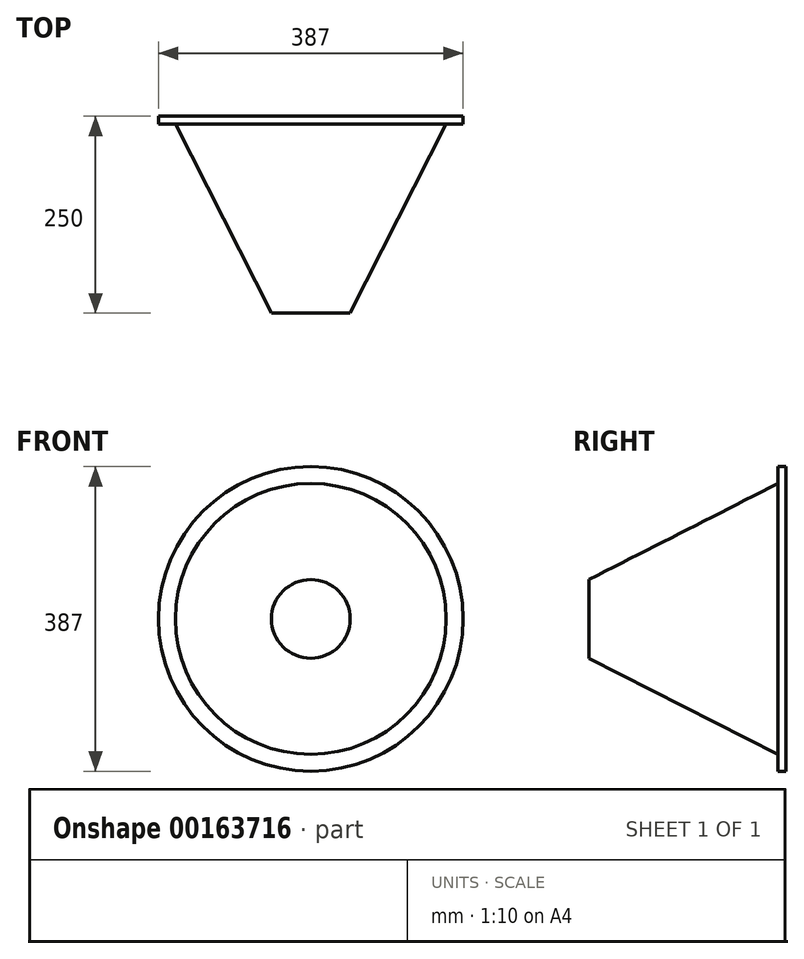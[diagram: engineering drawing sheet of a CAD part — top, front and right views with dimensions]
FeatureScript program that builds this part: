
annotation { "Feature Type Name" : "Feature", "Feature Type Description" : "" }
export const myFeature = defineFeature(function(context is Context, id is Id, definition is map)
    precondition{}
    {
        {
            var Q0;
            Q0=qCreatedBy(makeId("Front.planeOp"),FACE);
            var sketch = newSketch(context, id + "F0", { "sketchPlane" : qUnion([Q0])});
            skCircle(sketch, "E0", {"center": v(0, 0) * mm, "radius": 193.5 * mm});
            skSolve(sketch);
        }
        {
            var Q0;
            Q0 = qSketchRegion(id + "F0", true);
            extrude(context, id + "F1", {"entities" : qUnion([Q0]), "depth" : 10 * mm});
        }
        {
            var Q0;
            Q0=qCreatedBy(makeId("Top.planeOp"),FACE);
            var sketch = newSketch(context, id + "F2", { "sketchPlane" : qUnion([Q0])});
            skLineSegment(sketch, "E1", {"start": v(-172, -10) * mm, "end": v(0, -10) * mm});
            skLineSegment(sketch, "E2", {"start": v(0, -10) * mm, "end": v(0, -250) * mm});
            skLineSegment(sketch, "E3", {"start": v(0, -250) * mm, "end": v(-50, -250) * mm});
            skLineSegment(sketch, "E4", {"start": v(-50, -250) * mm, "end": v(-172, -10) * mm});
            skSolve(sketch);
        }
        {
            var Q0;
            Q0 = qSketchRegion(id + "F2", true);
            var Q1;
            Q1=sQuery(id+"F2.wireOp",EDGE,"E2");
            revolve(context, id + "F3", {"operationType" : NewBodyOperationType.ADD, "entities" : qUnion([Q0]), "axis" : qUnion([Q1]), "revolveType" : RevolveType.FULL});
        }
    });
